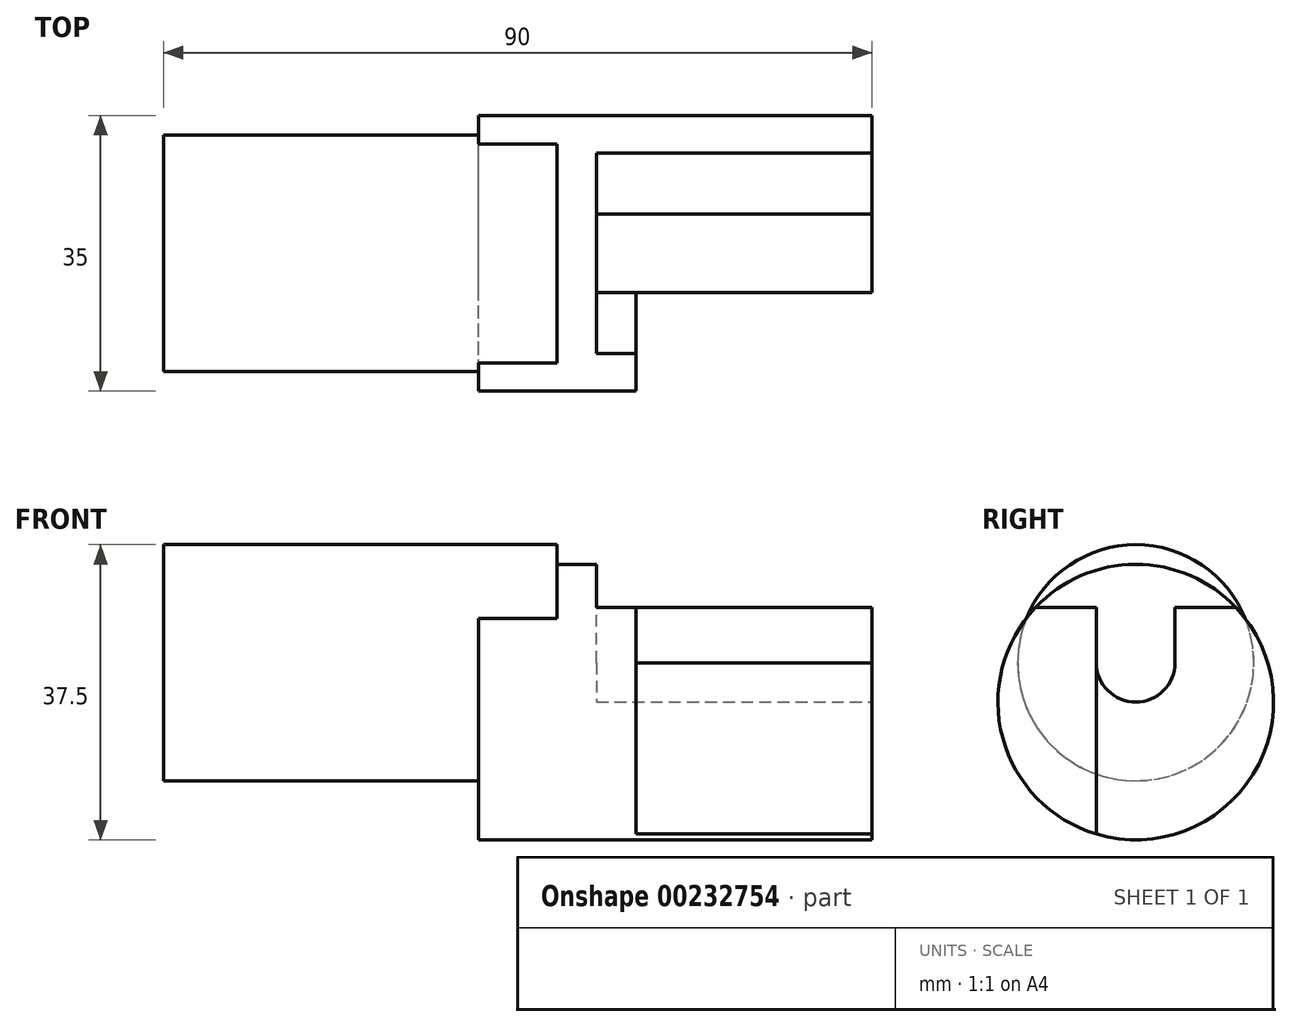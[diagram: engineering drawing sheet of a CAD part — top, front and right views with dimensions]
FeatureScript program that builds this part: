
annotation { "Feature Type Name" : "Feature", "Feature Type Description" : "" }
export const myFeature = defineFeature(function(context is Context, id is Id, definition is map)
    precondition{}
    {
        {
            var Q0;
            Q0=qCreatedBy(makeId("Right.planeOp"),FACE);
            var sketch = newSketch(context, id + "F0", { "sketchPlane" : qUnion([Q0])});
            skCircle(sketch, "E0", {"center": v(0, 0) * mm, "radius": 15 * mm});
            skSolve(sketch);
        }
        {
            var Q0;
            Q0=makeQuery(id+"F0.imprint","IMPRINT",FACE,{"disambiguationData":[TD([[makeQuery(id+"F0.imprint","IMPRINT",EDGE,{"derivedFrom":sQuery(id+"F0.wireOp",EDGE,"E0")}),1.0]])]});
            extrude(context, id + "F1", {"entities" : qUnion([Q0]), "depth" : 50 * mm});
        }
        {
            var Q0;
            Q0=makeQuery(id+"F1.opExtrude","CAP_FACE",FACE,{"disambiguationData":[OSD([sQuery(id+"F0.wireOp",EDGE,"E0")])],"isStart":false});
            var sketch = newSketch(context, id + "F2", { "sketchPlane" : qUnion([Q0])});
            skLineSegment(sketch, "E1", {"start": v(-17.02, -5) * mm, "end": v(24.45, -5) * mm, "construction": true});
            skLineSegment(sketch, "E2", {"start": v(0, 29.8) * mm, "end": v(0, -35.3) * mm, "construction": true});
            skCircle(sketch, "E3", {"center": v(0, -5) * mm, "radius": 17.5 * mm});
            skSolve(sketch);
        }
        {
            var Q0;
            {var subQ0=sQuery(id+"F2.wireOp",EDGE,"E3");var subQ1=makeQuery(id+"F1.opExtrude","CAP_EDGE",EDGE,{"disambiguationData":[OSD([sQuery(id+"F0.wireOp",EDGE,"E0")])],"isStart":false});var subQ2=makeQuery(id+"F2.imprint","INTERSECT",VERTEX,{"disambiguationData":[OD(0.0)],"derivedFrom":[subQ1,subQ0]});Q0=makeQuery(id+"F2.imprint","IMPRINT",FACE,{"disambiguationData":[TD([[makeQuery(id+"F2.imprint","IMPRINT",EDGE,{"disambiguationData":[TD([[subQ2,-1.0]])],"derivedFrom":subQ0}),1.0]])]});}
            extrude(context, id + "F3", {"entities" : qUnion([Q0]), "operationType" : NewBodyOperationType.ADD, "oppositeDirection" : true, "depth" : 10 * mm});
        }
        {
            var Q0;
            Q0 = qSketchRegion(id + "F2", true);
            extrude(context, id + "F4", {"entities" : qUnion([Q0]), "operationType" : NewBodyOperationType.ADD, "depth" : 40 * mm});
        }
        {
            var Q0;
            Q0=makeQuery(id+"F4.opExtrude","CAP_FACE",FACE,{"disambiguationData":[OSD([sQuery(id+"F2.wireOp",EDGE,"E3")])],"isStart":false});
            var sketch = newSketch(context, id + "F5", { "sketchPlane" : qUnion([Q0])});
            skSolve(sketch);
        }
        {
            var Q0;
            Q0=makeQuery(id+"F5.imprint","IMPRINT",FACE,{"disambiguationData":[TD([[makeQuery(id+"F5.imprint","IMPRINT",EDGE,{"derivedFrom":makeQuery(id+"F4.opExtrude","CAP_EDGE",EDGE,{"disambiguationData":[OSD([sQuery(id+"F2.wireOp",EDGE,"E3")])],"isStart":false})}),1.0]])]});
            var sketch = newSketch(context, id + "F6", { "sketchPlane" : qUnion([Q0])});
            skArc(sketch, "E4.0.0", {"start": v(-12.74, 7) * mm, "mid": v(0, -22.5) * mm, "end": v(12.74, 7) * mm, "construction": true});
            skLineSegment(sketch, "E5", {"start": v(-12.74, 7) * mm, "end": v(-5, 7) * mm});
            skArc(sketch, "E6", {"start": v(-5, 0) * mm, "mid": v(0, -5) * mm, "end": v(5, 0) * mm});
            skLineSegment(sketch, "E7", {"start": v(-5, 0) * mm, "end": v(-5, 7) * mm});
            skLineSegment(sketch, "E8", {"start": v(5, 0) * mm, "end": v(5, 7) * mm});
            skLineSegment(sketch, "E9.trimOffspring", {"start": v(5, 7) * mm, "end": v(12.74, 7) * mm});
            skLineSegment(sketch, "E10", {"start": v(-5, 0) * mm, "end": v(-5, -21.77) * mm});
            skSolve(sketch);
        }
        {
            var Q0;
            {var subQ1=sQuery(id+"F6.wireOp",EDGE,"E5");Q0=makeQuery(id+"F6.imprint","IMPRINT",FACE,{"disambiguationData":[TD([[makeQuery(id+"F6.imprint","IMPRINT",EDGE,{"derivedFrom":subQ1}),1.0]])]});}
            extrude(context, id + "F7", {"entities" : qUnion([Q0]), "operationType" : NewBodyOperationType.REMOVE, "oppositeDirection" : true, "depth" : 35 * mm});
        }
        {
            var Q0;
            {var subQ0=sQuery(id+"F6.wireOp",EDGE,"E5");Q0=makeQuery(id+"F6.imprint","IMPRINT",FACE,{"disambiguationData":[TD([[makeQuery(id+"F6.imprint","IMPRINT",EDGE,{"derivedFrom":subQ0}),-1.0]])]});}
            extrude(context, id + "F8", {"entities" : qUnion([Q0]), "operationType" : NewBodyOperationType.REMOVE, "oppositeDirection" : true, "depth" : 30 * mm});
        }
    });
